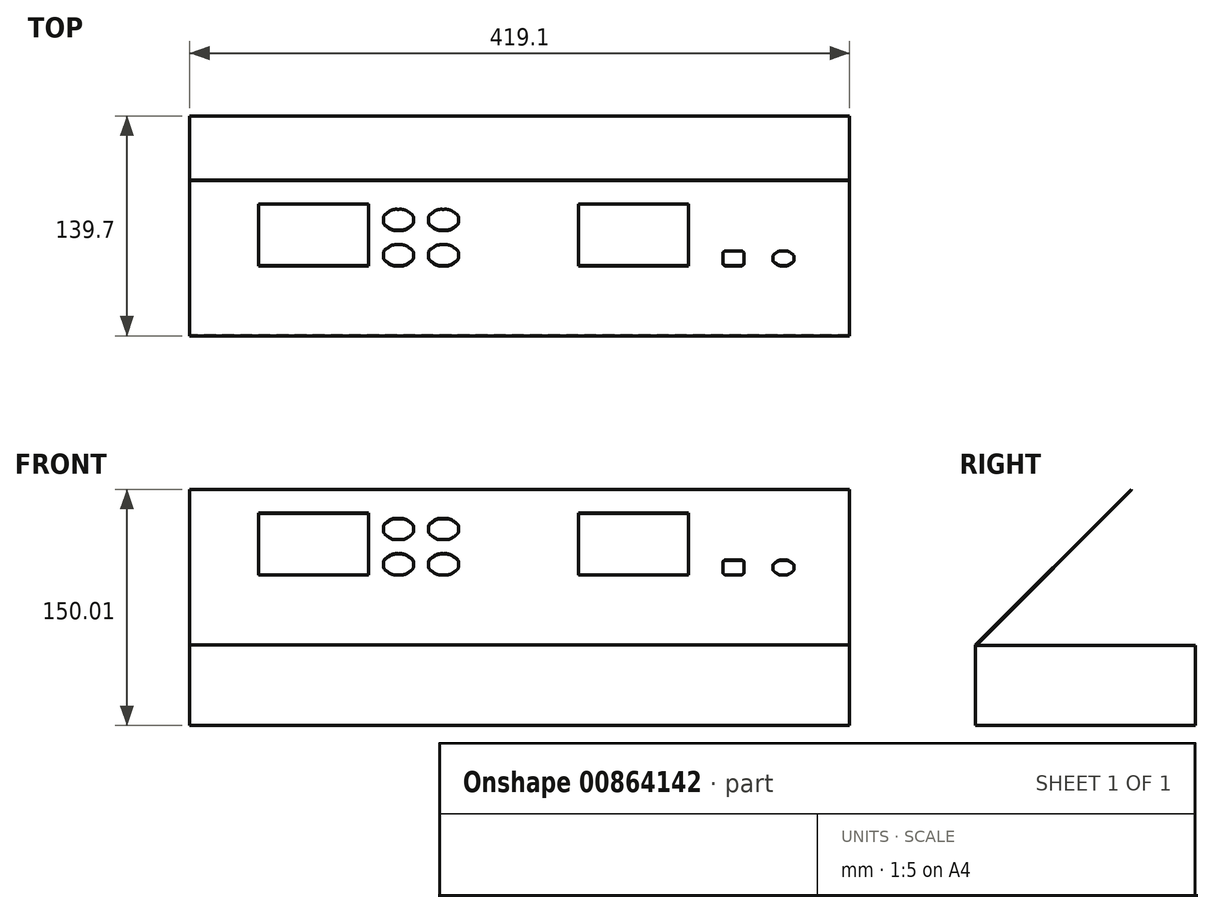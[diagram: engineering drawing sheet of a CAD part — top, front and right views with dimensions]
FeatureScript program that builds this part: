
annotation { "Feature Type Name" : "Feature", "Feature Type Description" : "" }
export const myFeature = defineFeature(function(context is Context, id is Id, definition is map)
    precondition{}
    {
        {
            var Q0;
            Q0=qCreatedBy(makeId("Right.planeOp"),FACE);
            var sketch = newSketch(context, id + "F0", { "sketchPlane" : qUnion([Q0])});
            skLineSegment(sketch, "E0.bottom", {"start": v(0, 0) * mm, "end": v(-139.7, 0) * mm});
            skLineSegment(sketch, "E0.top", {"start": v(0, 50.8) * mm, "end": v(-139.3, 50.8) * mm});
            skLineSegment(sketch, "E0.left", {"start": v(0, 0) * mm, "end": v(0, 50.8) * mm});
            skLineSegment(sketch, "E0.right", {"start": v(-139.7, 0) * mm, "end": v(-139.7, 51.22) * mm});
            skLineSegment(sketch, "E1", {"start": v(-139.7, 51.22) * mm, "end": v(-40.92, 150) * mm});
            skLineSegment(sketch, "E2", {"start": v(-40.92, 150) * mm, "end": v(-40.63, 149.72) * mm});
            skLineSegment(sketch, "E3", {"start": v(-40.63, 149.72) * mm, "end": v(-139.3, 51.05) * mm});
            skLineSegment(sketch, "E4", {"start": v(-139.3, 50.8) * mm, "end": v(-139.3, 51.05) * mm});
            skLineSegment(sketch, "E5", {"start": v(-139.3, 50.8) * mm, "end": v(-139.7, 50.8) * mm, "construction": true});
            skSolve(sketch);
        }
        {
            var Q0;
            Q0=qSketchRegion(id+"F0",true);
            extrude(context, id + "F1", {"entities" : qUnion([Q0]), "endBound" : BoundingType.SYMMETRIC, "depth" : 419.1 * mm, "offsetDistance" : 25.4 * mm});
        }
        {
            var Q0;
            Q0=makeQuery(id+"F1.opExtrude","SWEPT_FACE",FACE,{"disambiguationData":[OSD([sQuery(id+"F0.wireOp",EDGE,"E1")])]});
            var sketch = newSketch(context, id + "F2", { "sketchPlane" : qUnion([Q0])});
            skLineSegment(sketch, "E6", {"start": v(-96.08, 0.3) * mm, "end": v(-96.08, 55.86) * mm});
            skLineSegment(sketch, "E7", {"start": v(-96.08, 55.86) * mm, "end": v(-165.93, 55.86) * mm});
            skLineSegment(sketch, "E8", {"start": v(-165.93, 55.86) * mm, "end": v(-165.93, 0.3) * mm});
            skLineSegment(sketch, "E9", {"start": v(-165.93, 0.3) * mm, "end": v(-96.08, 0.3) * mm});
            skLineSegment(sketch, "E10", {"start": v(-210.38, -63.2) * mm, "end": v(-210.38, 75.7) * mm, "construction": true});
            skLineSegment(sketch, "E11", {"start": v(37.28, 55.86) * mm, "end": v(37.28, 0.3) * mm});
            skLineSegment(sketch, "E12", {"start": v(128.96, 11.41) * mm, "end": v(128.96, 2.68) * mm});
            skLineSegment(sketch, "E13", {"start": v(208.71, -63.2) * mm, "end": v(208.71, 75.7) * mm, "construction": true});
            skLineSegment(sketch, "E14", {"start": v(107.13, 0.3) * mm, "end": v(107.13, 55.86) * mm});
            skLineSegment(sketch, "E15", {"start": v(140.07, 13.8) * mm, "end": v(131.34, 13.8) * mm});
            skLineSegment(sketch, "E16", {"start": v(131.34, 0.3) * mm, "end": v(140.07, 0.3) * mm});
            skLineSegment(sketch, "E17", {"start": v(142.45, 2.68) * mm, "end": v(142.45, 11.41) * mm});
            skLineSegment(sketch, "E18", {"start": v(107.13, 6.55) * mm, "end": v(107.13, 32.95) * mm});
            skLineSegment(sketch, "E19", {"start": v(107.13, 55.86) * mm, "end": v(37.28, 55.86) * mm});
            skLineSegment(sketch, "E20", {"start": v(37.28, 0.3) * mm, "end": v(107.13, 0.3) * mm});
            skLineSegment(sketch, "E21", {"start": v(-210.38, 75.7) * mm, "end": v(208.71, 75.7) * mm, "construction": true});
            skLineSegment(sketch, "E22", {"start": v(208.71, -63.2) * mm, "end": v(-210.38, -63.2) * mm, "construction": true});
            skFitSpline(sketch, "E23", {"points": [v(-77.03, 51.1) * mm, v(-79.53, 51.1) * mm, v(-82, 50.08) * mm, v(-83.77, 48.31) * mm, v(-85.53, 46.55) * mm, v(-86.56, 44.07) * mm, v(-86.56, 41.58) * mm, v(-86.56, 39.08) * mm, v(-85.53, 36.6) * mm, v(-83.77, 34.84) * mm]});
            skFitSpline(sketch, "E24", {"points": [v(-83.77, 34.84) * mm, v(-82, 33.08) * mm, v(-79.53, 32.05) * mm, v(-77.03, 32.05) * mm, v(-74.54, 32.05) * mm, v(-72.06, 33.08) * mm, v(-70.3, 34.84) * mm]});
            skFitSpline(sketch, "E25", {"points": [v(-70.3, 34.84) * mm, v(-68.54, 36.6) * mm, v(-67.5, 39.08) * mm, v(-67.5, 41.58) * mm, v(-67.5, 44.07) * mm, v(-68.54, 46.55) * mm, v(-70.3, 48.31) * mm]});
            skFitSpline(sketch, "E26", {"points": [v(-70.3, 48.31) * mm, v(-72.06, 50.08) * mm, v(-74.54, 51.1) * mm, v(-77.03, 51.1) * mm]});
            skFitSpline(sketch, "E27", {"points": [v(-77.03, 19.35) * mm, v(-79.53, 19.35) * mm, v(-82, 18.33) * mm, v(-83.77, 16.56) * mm, v(-85.53, 14.8) * mm, v(-86.56, 12.32) * mm, v(-86.56, 9.83) * mm, v(-86.56, 7.33) * mm, v(-85.53, 4.86) * mm, v(-83.77, 3.1) * mm]});
            skFitSpline(sketch, "E28", {"points": [v(-83.77, 3.1) * mm, v(-82, 1.33) * mm, v(-79.53, 0.3) * mm, v(-77.03, 0.3) * mm, v(-74.54, 0.3) * mm, v(-72.06, 1.33) * mm, v(-70.3, 3.1) * mm]});
            skFitSpline(sketch, "E29", {"points": [v(-70.3, 3.1) * mm, v(-68.54, 4.86) * mm, v(-67.5, 7.33) * mm, v(-67.5, 9.83) * mm, v(-67.5, 12.32) * mm, v(-68.54, 14.8) * mm, v(-70.3, 16.56) * mm]});
            skFitSpline(sketch, "E30", {"points": [v(-70.3, 16.56) * mm, v(-72.06, 18.33) * mm, v(-74.54, 19.35) * mm, v(-77.03, 19.35) * mm]});
            skFitSpline(sketch, "E31", {"points": [v(-48.44, 19.35) * mm, v(-50.94, 19.35) * mm, v(-53.42, 18.33) * mm, v(-55.18, 16.56) * mm, v(-56.94, 14.8) * mm, v(-57.97, 12.32) * mm, v(-57.97, 9.83) * mm, v(-57.97, 7.33) * mm, v(-56.94, 4.86) * mm, v(-55.18, 3.1) * mm]});
            skFitSpline(sketch, "E32", {"points": [v(-55.18, 3.1) * mm, v(-53.42, 1.33) * mm, v(-50.94, 0.3) * mm, v(-48.44, 0.3) * mm, v(-45.95, 0.3) * mm, v(-43.47, 1.33) * mm, v(-41.7, 3.1) * mm]});
            skFitSpline(sketch, "E33", {"points": [v(-41.7, 3.1) * mm, v(-39.95, 4.86) * mm, v(-38.92, 7.33) * mm, v(-38.92, 9.83) * mm, v(-38.92, 12.32) * mm, v(-39.95, 14.8) * mm, v(-41.7, 16.56) * mm]});
            skFitSpline(sketch, "E34", {"points": [v(-41.7, 16.56) * mm, v(-43.47, 18.33) * mm, v(-45.95, 19.35) * mm, v(-48.44, 19.35) * mm]});
            skFitSpline(sketch, "E35", {"points": [v(-48.44, 51.1) * mm, v(-50.94, 51.1) * mm, v(-53.42, 50.08) * mm, v(-55.18, 48.31) * mm, v(-56.94, 46.55) * mm, v(-57.97, 44.07) * mm, v(-57.97, 41.58) * mm, v(-57.97, 39.08) * mm, v(-56.94, 36.6) * mm, v(-55.18, 34.84) * mm]});
            skFitSpline(sketch, "E36", {"points": [v(-55.18, 34.84) * mm, v(-53.42, 33.08) * mm, v(-50.94, 32.05) * mm, v(-48.44, 32.05) * mm, v(-45.95, 32.05) * mm, v(-43.47, 33.08) * mm, v(-41.7, 34.84) * mm]});
            skFitSpline(sketch, "E37", {"points": [v(-41.7, 34.84) * mm, v(-39.95, 36.6) * mm, v(-38.92, 39.08) * mm, v(-38.92, 41.58) * mm, v(-38.92, 44.07) * mm, v(-39.95, 46.55) * mm, v(-41.7, 48.31) * mm]});
            skFitSpline(sketch, "E38", {"points": [v(-41.7, 48.31) * mm, v(-43.47, 50.08) * mm, v(-45.95, 51.1) * mm, v(-48.44, 51.1) * mm]});
            skFitSpline(sketch, "E39", {"points": [v(128.96, 2.68) * mm, v(128.96, 2.06) * mm, v(129.22, 1.44) * mm, v(129.66, 1) * mm]});
            skFitSpline(sketch, "E40", {"points": [v(129.66, 1) * mm, v(130.1, 0.56) * mm, v(130.72, 0.3) * mm, v(131.34, 0.3) * mm]});
            skFitSpline(sketch, "E41", {"points": [v(131.34, 13.8) * mm, v(130.72, 13.8) * mm, v(130.1, 13.54) * mm, v(129.66, 13.1) * mm]});
            skFitSpline(sketch, "E42", {"points": [v(129.66, 13.1) * mm, v(129.22, 12.66) * mm, v(128.96, 12.04) * mm, v(128.96, 11.41) * mm]});
            skFitSpline(sketch, "E43", {"points": [v(167.46, 13.8) * mm, v(165.69, 13.8) * mm, v(163.93, 13.07) * mm, v(162.69, 11.82) * mm]});
            skFitSpline(sketch, "E44", {"points": [v(162.69, 11.82) * mm, v(161.44, 10.57) * mm, v(160.7, 8.82) * mm, v(160.7, 7.05) * mm, v(160.7, 5.28) * mm, v(161.44, 3.53) * mm, v(162.69, 2.28) * mm]});
            skFitSpline(sketch, "E45", {"points": [v(162.69, 2.28) * mm, v(163.93, 1.03) * mm, v(165.69, 0.3) * mm, v(167.46, 0.3) * mm, v(169.22, 0.3) * mm, v(170.98, 1.03) * mm, v(172.23, 2.28) * mm]});
            skFitSpline(sketch, "E46", {"points": [v(172.23, 2.28) * mm, v(173.48, 3.53) * mm, v(174.2, 5.28) * mm, v(174.2, 7.05) * mm, v(174.2, 8.82) * mm, v(173.48, 10.57) * mm, v(172.23, 11.82) * mm]});
            skFitSpline(sketch, "E47", {"points": [v(172.23, 11.82) * mm, v(170.98, 13.07) * mm, v(169.22, 13.8) * mm, v(167.46, 13.8) * mm]});
            skFitSpline(sketch, "E48", {"points": [v(142.45, 11.41) * mm, v(142.45, 12.04) * mm, v(142.2, 12.66) * mm, v(141.75, 13.1) * mm, v(141.31, 13.54) * mm, v(140.7, 13.8) * mm, v(140.07, 13.8) * mm]});
            skFitSpline(sketch, "E49", {"points": [v(140.07, 0.3) * mm, v(140.7, 0.3) * mm, v(141.31, 0.56) * mm, v(141.75, 1) * mm]});
            skFitSpline(sketch, "E50", {"points": [v(141.75, 1) * mm, v(142.2, 1.44) * mm, v(142.45, 2.06) * mm, v(142.45, 2.68) * mm]});
            skSolve(sketch);
        }
        {
            var Q0;
            Q0=qSketchRegion(id+"F2",true);
            var Q1;
            Q1=makeQuery(id+"F1.opExtrude","SWEPT_FACE",FACE,{"disambiguationData":[OSD([sQuery(id+"F0.wireOp",EDGE,"E3")])]});
            extrude(context, id + "F3", {"entities" : qUnion([Q0]), "operationType" : NewBodyOperationType.REMOVE, "endBound" : BoundingType.UP_TO_SURFACE, "oppositeDirection" : true, "depth" : 25.4 * mm, "endBoundEntityFace" : qUnion([Q1]), "offsetDistance" : 25.4 * mm});
        }
    });
